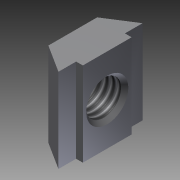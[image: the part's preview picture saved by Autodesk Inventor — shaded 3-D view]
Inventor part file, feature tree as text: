
AUTODESK INVENTOR PART (.ipt)
format: ipt  version: 2011 SP1 (Build 150282100, 282)  size: 102,912 bytes
history: native  units: mm
features: other x21, sketch x2, extrude x1, revolve x1, thread x1
ambient origin geometry x8: Origin, YZ Plane, XZ Plane, XY Plane, X Axis, Y Axis, Z Axis, Center Point
bodies: Solid1 (feature_tree)
feature tree (26):
  extrude  "Extrusion1"  TaperAngle=360.0deg  [1 undecoded]
  revolve  "Revolution1"  [1 undecoded]
  thread  "Thread1"  [1 undecoded]
  other  "nut_XY"
  other  "nut_YZ"
  other  "nut_ZX"
  other  "nut_X"
  other  "nut_Y"
  other  "nut_Z"
  other  "nut_Center"
  other  "to_bolt_XY"
  other  "to_bolt_YZ"
  other  "to_bolt_ZX"
  other  "to_bolt_X"
  other  "to_bolt_Y"
  other  "to_bolt_Z"
  other  "to_bolt_Center"
  other  "to_frames_XY"
  other  "to_frames_YZ"
  other  "to_frames_ZX"
  other  "to_frames_X"
  other  "to_frames_Y"
  other  "to_frames_Z"
  other  "to_frames_Center"
  sketch  "Sketch_4"  dims[d0=10.0mm d1=0.0mm d2=360.0deg]
  sketch  "Sketch_5"  dims[d3=3.234mm d4=0.0mm]
note: 3 required parameter values undecoded (feature->parameter linkage not recoverable at this tier; creation-order binding heuristic only, values carry confidence <= 0.55)
